# Revit family: NLRS_63_LF_UN_noodverlichting HEN400 plafondmontage_htk
name_source: partatom
category: Lighting Fixtures
units: mm (PartAtom-declared; Revit-internal decimal feet)

## family parameters
Always vertical = Yes
Cut with Voids When Loaded = No
Light Source = Yes
OmniClass Number = 23.85.30.21
OmniClass Title = Environmental Detection/Registration
Part Type = Normal
Room Calculation Point = No
Round Connector Dimension = Use Radius
Shared = No
Work Plane-Based = No

## types (2) — shared parameters
Apparent Load = 2 VA
Color Filter = 16777215
Dimming Lamp Color Temperature Shift = <None>
Emit from Line Length = 610 mm
Lamp = LED
Manufacturer = Hertek
NLRS_C_breedte = 60 mm  [stored 0.19685 ft]
NLRS_C_code_fabrikant_gln = 8714253082646
NLRS_C_hoogte = 170 mm  [stored 0.557743 ft]
NLRS_C_lengte = 340 mm  [stored 1.11549 ft]
NLRS_C_materiaal = Polycarbonaat wit
NLRS_C_materiaal_01 = Glass
NLRS_C_materiaal_kleur = wit
NLRS_C_model = HEN400 dec AT
NLRS_C_revit_versie = 2020
NLRS_E_c01_radius = 8 mm  [stored 0.0262467 ft]
NLRS_E_c01_schijnbaar_vermogen = 2 VA
NLRS_E_c01_schijnbaar_vermogen_fase_1 = 0 VA
NLRS_E_c01_schijnbaar_vermogen_fase_2 = 0 VA
NLRS_E_c01_schijnbaar_vermogen_fase_3 = 0 VA
NLRS_E_spanning = 230 V
NLRS_E_stroom = 0.0 A
NLRS_S_gewicht_netto = 0.08 kg
URL = https://www.hertek.nl
batterij = 4.8V/0.6Ah NiMH (High temp)
centraal = No
decentraal = Yes
plafondmontage = Yes
vermogensclassificatie = NV
wireless = No
zichtbaar_01 = No
zero-valued in all types: Default Elevation

## per-type parameters (varying)
| type | NLRS_C_code_artikel | NLRS_C_omschrijving | Photometric Web File | Tilt Angle | picto | transparante kap HED421 |
| HEN400 economy dec. vluchtwegaanduiding 230v plafondmontage_htk_HED421X | HED421X | HEN400 dec AT universeel picto 10/8YW | generic | 60.00° | Yes | No |
| HEN400 economy dec. vluchtwegverlichting 230v_htk_HED451X | HED451X | HEN400 dec AT universeel nood 10/8YW | HED151_LDT.ies | 90.00° | No | Yes |

note: [stored X ft] marks values corroborated as IEEE doubles in the binary element streams (Revit-internal decimal feet)

## geometry (parser evidence)
native form markers: Blend x10, Sweep x59
no freeform markers — native parametric forms only
